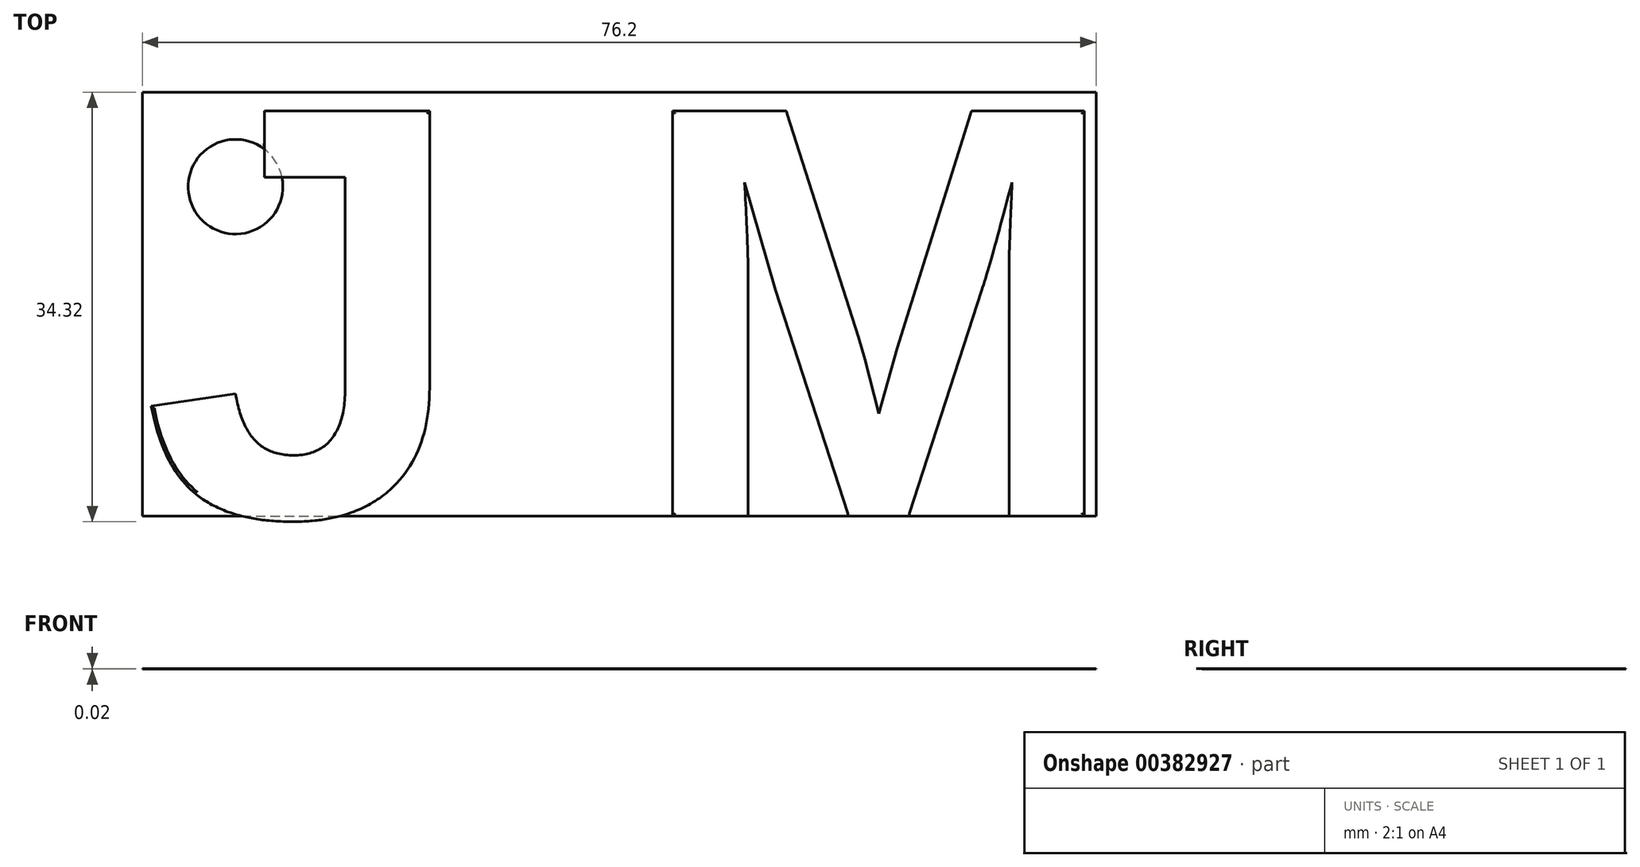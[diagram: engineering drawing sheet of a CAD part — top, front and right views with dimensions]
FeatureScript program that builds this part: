
annotation { "Feature Type Name" : "Feature", "Feature Type Description" : "" }
export const myFeature = defineFeature(function(context is Context, id is Id, definition is map)
    precondition{}
    {
        {
            var Q0;
            Q0=qCreatedBy(makeId("Top.planeOp"),FACE);
            var sketch = newSketch(context, id + "F0", { "sketchPlane" : qUnion([Q0])});
            skLineSegment(sketch, "E0.bottom", {"start": v(-29.03, -29.77) * mm, "end": v(47.17, -29.77) * mm});
            skLineSegment(sketch, "E0.top", {"start": v(-29.03, 4.1) * mm, "end": v(47.17, 4.1) * mm});
            skLineSegment(sketch, "E0.left", {"start": v(-29.03, -29.77) * mm, "end": v(-29.03, 4.1) * mm});
            skLineSegment(sketch, "E0.right", {"start": v(47.17, -29.77) * mm, "end": v(47.17, 4.1) * mm});
            skSolve(sketch);
        }
        {
            var Q0;
            Q0=makeQuery(id+"F0.imprint","IMPRINT",FACE,{"disambiguationData":[TD([[makeQuery(id+"F0.imprint","IMPRINT",EDGE,{"derivedFrom":sQuery(id+"F0.wireOp",EDGE,"E0.bottom")}),1.0]])]});
            extrude(context, id + "F1", {"entities" : qUnion([Q0]), "depth" : 1 / 76.2 * mm});
        }
        {
            var Q0;
            Q0=makeQuery(id+"F1.opExtrude","CAP_FACE",FACE,{"disambiguationData":[OSD([sQuery(id+"F0.wireOp",EDGE,"E0.bottom"),sQuery(id+"F0.wireOp",EDGE,"E0.top"),sQuery(id+"F0.wireOp",EDGE,"E0.left"),sQuery(id+"F0.wireOp",EDGE,"E0.right")])],"isStart":false});
            var sketch = newSketch(context, id + "F2", { "sketchPlane" : qUnion([Q0])});
            skCircle(sketch, "E1", {"center": v(-21.59, -3.45) * mm, "radius": 3.79 * mm});
            skSolve(sketch);
        }
        {
            var Q0;
            Q0=makeQuery(id+"F2.imprint","IMPRINT",FACE,{"disambiguationData":[TD([[makeQuery(id+"F2.imprint","IMPRINT",EDGE,{"derivedFrom":sQuery(id+"F2.wireOp",EDGE,"E1")}),1.0]])]});
            extrude(context, id + "F3", {"entities" : qUnion([Q0]), "operationType" : NewBodyOperationType.REMOVE, "oppositeDirection" : true, "depth" : 25.4 * mm});
        }
        {
            var Q0;
            Q0=makeQuery(id+"F1.opExtrude","CAP_FACE",FACE,{"disambiguationData":[OSD([sQuery(id+"F0.wireOp",EDGE,"E0.bottom"),sQuery(id+"F0.wireOp",EDGE,"E0.top"),sQuery(id+"F0.wireOp",EDGE,"E0.left"),sQuery(id+"F0.wireOp",EDGE,"E0.right")])],"isStart":false});
            var sketch = newSketch(context, id + "F4", { "sketchPlane" : qUnion([Q0])});
            skText(sketch, "E2", { "text": "J M", "fontName": "Arimo-Bold.ttf"});
            const initialGuessF4  = {"E2": [-0.02903, -0.02977, 1, 0, 0.03387]};
            skSetInitialGuess(sketch, initialGuessF4);
            skSolve(sketch);
        }
        {
            var Q0;
            Q0 = qSketchRegion(id + "F4", true);
            extrude(context, id + "F5", {"entities" : qUnion([Q0]), "operationType" : NewBodyOperationType.ADD, "depth" : 1 / 254 * mm});
        }
        {
            var Q0;
            Q0=makeQuery(id+"F5.opExtrude","CAP_FACE",FACE,{"disambiguationData":[OSD([sQuery(id+"F4.wireOp",EDGE,"E2.sketch_text.stroke-0"),sQuery(id+"F4.wireOp",EDGE,"E2.sketch_text.stroke-1"),sQuery(id+"F4.wireOp",EDGE,"E2.sketch_text.stroke-2"),sQuery(id+"F4.wireOp",EDGE,"E2.sketch_text.stroke-3"),sQuery(id+"F4.wireOp",EDGE,"E2.sketch_text.stroke-4"),sQuery(id+"F4.wireOp",EDGE,"E2.sketch_text.stroke-5"),sQuery(id+"F4.wireOp",EDGE,"E2.sketch_text.stroke-6"),sQuery(id+"F4.wireOp",EDGE,"E2.sketch_text.stroke-7"),sQuery(id+"F4.wireOp",EDGE,"E2.sketch_text.stroke-8"),sQuery(id+"F4.wireOp",EDGE,"E2.sketch_text.stroke-9"),sQuery(id+"F4.wireOp",EDGE,"E2.sketch_text.stroke-10"),sQuery(id+"F4.wireOp",EDGE,"E2.sketch_text.stroke-11"),sQuery(id+"F4.wireOp",EDGE,"E2.sketch_text.stroke-12"),sQuery(id+"F4.wireOp",EDGE,"E2.sketch_text.stroke-13")])],"isStart":false});
            var sketch = newSketch(context, id + "F6", { "sketchPlane" : qUnion([Q0])});
            skLineSegment(sketch, "E3", {"start": v(-19.3, 0) * mm, "end": v(-17.95, -2.72) * mm});
            skLineSegment(sketch, "E4", {"start": v(-19.3, 0) * mm, "end": v(-19.3, -2.72) * mm});
            skLineSegment(sketch, "E5", {"start": v(-19.3, -2.72) * mm, "end": v(-17.95, -2.72) * mm});
            skSolve(sketch);
        }
        {
            var Q0;
            Q0=makeQuery(id+"F6.imprint","IMPRINT",FACE,{"disambiguationData":[TD([[makeQuery(id+"F6.imprint","IMPRINT",EDGE,{"derivedFrom":sQuery(id+"F6.wireOp",EDGE,"E3")}),-1.0]])]});
            extrude(context, id + "F7", {"entities" : qUnion([Q0]), "operationType" : NewBodyOperationType.REMOVE, "oppositeDirection" : true, "depth" : 25.4 * mm});
        }
        {
            var Q0;
            Q0=makeQuery(id+"F5.opExtrude","CAP_EDGE",EDGE,{"disambiguationData":[OSD([sQuery(id+"F4.wireOp",EDGE,"E2.sketch_text.stroke-11")])],"isStart":false});
            var Q1;
            Q1=makeQuery(id+"F5.opExtrude","CAP_EDGE",EDGE,{"disambiguationData":[OSD([sQuery(id+"F4.wireOp",EDGE,"E2.sketch_text.stroke-10")])],"isStart":false});
            var Q2;
            Q2=makeQuery(id+"F5.opExtrude","CAP_EDGE",EDGE,{"disambiguationData":[OSD([sQuery(id+"F4.wireOp",EDGE,"E2.sketch_text.stroke-2")])],"isStart":false});
            fillet(context, id + "F8", {"entities" : qUnion([Q0, Q1, Q2]), "radius" : 5.08 * mm, "tangentPropagation" : true, "allowEdgeOverflow" : false});
        }
        {
            var Q0;
            Q0=makeQuery(id+"F5.boolean.opBoolean","MERGE",FACE,{"derivedFrom":[makeQuery(id+"F1.opExtrude","SWEPT_FACE",FACE,{"disambiguationData":[OSD([sQuery(id+"F0.wireOp",EDGE,"E0.bottom")])]}),makeQuery(id+"F5.opExtrude","SWEPT_FACE",FACE,{"disambiguationData":[OSD([sQuery(id+"F4.wireOp",EDGE,"E2.sketch_text.stroke-19")])]}),makeQuery(id+"F5.opExtrude","SWEPT_FACE",FACE,{"disambiguationData":[OSD([sQuery(id+"F4.wireOp",EDGE,"E2.sketch_text.stroke-24")])]}),makeQuery(id+"F5.opExtrude","SWEPT_FACE",FACE,{"disambiguationData":[OSD([sQuery(id+"F4.wireOp",EDGE,"E2.sketch_text.stroke-34")])]})]});
            var sketch = newSketch(context, id + "F9", { "sketchPlane" : qUnion([Q0])});
            skLineSegment(sketch, "E6.bottom", {"start": v(-29.03, 0) * mm, "end": v(47.17, 0) * mm});
            skLineSegment(sketch, "E6.top", {"start": v(-29.03, 8.47) * mm, "end": v(47.17, 8.47) * mm});
            skLineSegment(sketch, "E6.left", {"start": v(-29.03, 0) * mm, "end": v(-29.03, 8.47) * mm});
            skLineSegment(sketch, "E6.right", {"start": v(47.17, 0) * mm, "end": v(47.17, 8.47) * mm});
            skSolve(sketch);
        }
        {
            var Q0;
            Q0=makeQuery(id+"F9.imprint","IMPRINT",FACE,{"disambiguationData":[TD([[makeQuery(id+"F9.imprint","IMPRINT",EDGE,{"derivedFrom":sQuery(id+"F9.wireOp",EDGE,"E6.bottom")}),1.0]])]});
            extrude(context, id + "F10", {"entities" : qUnion([Q0]), "operationType" : NewBodyOperationType.ADD, "depth" : 1 / 203.2 * mm});
        }
        {
            var Q0;
            Q0=makeQuery(id+"F5.opExtrude","CAP_EDGE",EDGE,{"disambiguationData":[OSD([sQuery(id+"F4.wireOp",EDGE,"E2.sketch_text.stroke-24")])],"isStart":false});
            var Q1;
            Q1=makeQuery(id+"F5.opExtrude","CAP_EDGE",EDGE,{"disambiguationData":[OSD([sQuery(id+"F4.wireOp",EDGE,"E2.sketch_text.stroke-19")])],"isStart":false});
            var Q2;
            Q2=makeQuery(id+"F5.opExtrude","CAP_EDGE",EDGE,{"disambiguationData":[OSD([sQuery(id+"F4.wireOp",EDGE,"E2.sketch_text.stroke-34")])],"isStart":false});
            var Q3;
            Q3=makeQuery(id+"F5.opExtrude","CAP_EDGE",EDGE,{"disambiguationData":[OSD([sQuery(id+"F4.wireOp",EDGE,"E2.sketch_text.stroke-33")])],"isStart":false});
            var Q4;
            Q4=makeQuery(id+"F5.opExtrude","CAP_EDGE",EDGE,{"disambiguationData":[OSD([sQuery(id+"F4.wireOp",EDGE,"E2.sketch_text.stroke-32")])],"isStart":false});
            var Q5;
            Q5=makeQuery(id+"F5.opExtrude","CAP_EDGE",EDGE,{"disambiguationData":[OSD([sQuery(id+"F4.wireOp",EDGE,"E2.sketch_text.stroke-26")])],"isStart":false});
            var Q6;
            Q6=makeQuery(id+"F5.opExtrude","CAP_EDGE",EDGE,{"disambiguationData":[OSD([sQuery(id+"F4.wireOp",EDGE,"E2.sketch_text.stroke-25")])],"isStart":false});
            fillet(context, id + "F11", {"entities" : qUnion([Q0, Q1, Q2, Q3, Q4, Q5, Q6]), "radius" : 5.08 * mm, "tangentPropagation" : true, "allowEdgeOverflow" : false});
        }
    });
